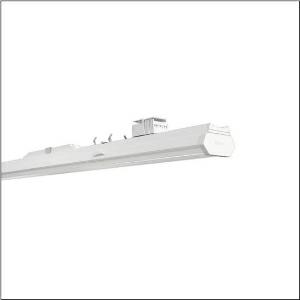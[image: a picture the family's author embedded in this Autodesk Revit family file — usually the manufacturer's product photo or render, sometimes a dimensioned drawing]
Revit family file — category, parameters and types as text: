
# Revit family: licross_r__21_protected_ho_52tp13cn4c5s_cd4a
name_source: partatom
category: Lighting Fixtures
units: mm (PartAtom-declared; Revit-internal decimal feet)

## family parameters
Cut with Voids When Loaded = No
Host = Face
Light Source = No
Part Type = Normal
Room Calculation Point = No
Round Connector Dimension = Use Diameter
Shared = No

## types (1)
- --- (1 x LED, 12680 lm, 68.9 W, 4000K)
    Apparent Load = 69 VA
    CIE Flux Codes = 89 96 99 100 99
    Color Rendering = 80
    Color Temperature = 4000K
    Default Elevation = 1800 mm
    Description = Licross® 21 Protected HO, luminaire insert, of sheet steel, galvanised, coil coated, white, length: 1.500mm, width: 66mm, height: 67mm, LED rated luminous flux: 12.690lm, light colour: 840, control gear: ON/OFF Multilumen, CLOi, control gear: ECG Multilumen, with plug, 3-pole, with phase selection, mains connection: 220..240V, AC, 50/60Hz, start of lifetime: 69W, end of service life: 83W, internal wiring halogen-free, primary light control with lens, of plastic, primary optical cover: cover, of PMMA, light emission: direct distribution, primary light characteristic: symmetric, protection rating (complete): IP64, insulation class (complete): insulation class I (protective earthing), certification: CE, ENEC, VDE, UKCA, protection symbol: D if used in an environment with conductive dust loads with corresponding accessories, impact resistance: IK06, permissible ambient temperature for indoor applications: -35..+35°C, corresponds to IFS (International Featured Standards) requirements for safety and quality in the food industry, reducing of maximum allowable ambient temperature of 5°C with ceiling mounting, LABS conformity tested according to VDMA 24364:2018-05, packaging unit: 1 piece
    Height = 92 mm
    Lamp = 1 x LED
    Lamp Light Flux = 12680 lm
    Lamp Power = 68.9 W
    Lamp count = 1
    Length = 1500 mm
    Luminous efficacy = 184 lm/W
    Manufacturer = Siteco
    ModVariant = No
    Model = 52TP13CN4C5S
    Mounting Place = Ceiling
    Mounting Type = Pendant
    Number of Poles = 1
    OnlyDefault = Yes
    Power Factor = 1
    Product Name = Licross® 21 Protected HO
    Product group = luminaire insert | ceiling pendant
    ProductGroupID = 902
    Protection Class = Protection class I
    Protection Degree = IP 64
    RLX_Detail_Level = 1
    RLX_Emergency_Light_Flux = 0 lm
    RLX_Emergency_Type = 0
    RLX_Emergency_Type_DB = No
    RlxData = <blob elided: 22029 chars, md5=ef2cb523>
    Socket = socket
    Standby Power = 0 W
    System Light Flux = 12680 lm
    System Power = 69 W
    Type Comments = factory setting: luminous flux: 100 % | (A | C | E) | 162 mA
    Type Image = l_1256148.jpg
    URL = http://relux.com
    VarID = @adj_132307
    Voltage = 0 V
    Weight = 0.00 kg
    Width = 88 mm

## geometry (parser evidence)
native form markers: Blend x4, Sweep x11
no freeform markers — native parametric forms only
